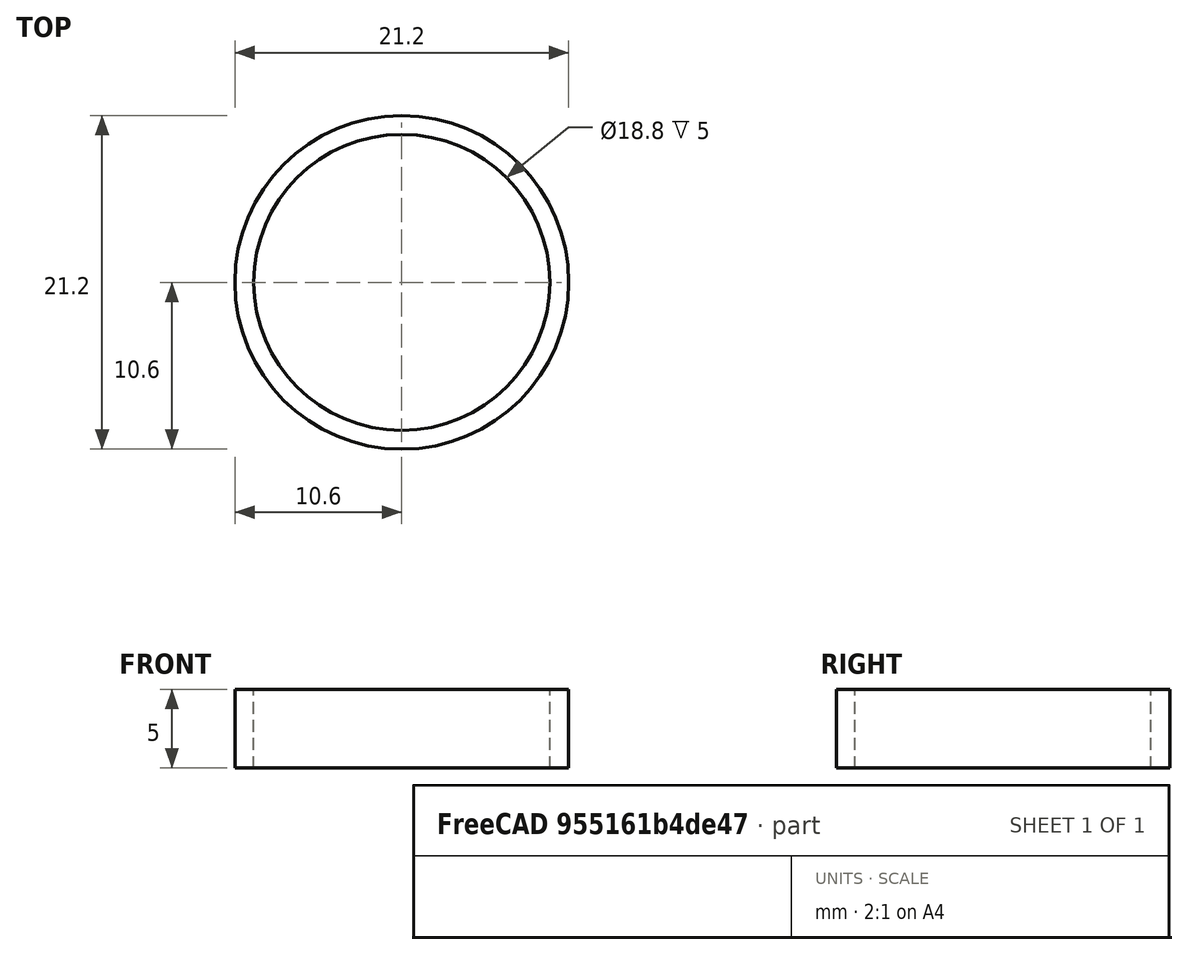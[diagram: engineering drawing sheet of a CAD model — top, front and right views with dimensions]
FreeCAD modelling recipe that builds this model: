
FCSTD DOCUMENT  (FreeCAD 0.20R29177 +426 (Git))
Label: Mag_AG_Outer
License: All rights reserved
LicenseURL: http://en.wikipedia.org/wiki/All_rights_reserved
objects: Sketcher::SketchObject×1, PartDesign::Revolution×1, PartDesign::Body×1
note: 4 computed .brp shape members not serialized (recipe doc carries the construction recipe); baked Part::Feature solids carry a one-line shape summary decoded from their .brp

FEATURE [Sketcher::SketchObject] Sketch
  FullyConstrained = true
  MapMode = 5
  Placement = pos=(0,0,0) rot=(1,0,0;1.5708rad)
  Support = -> [XZ_Plane]
  sketch-geometry (4):
    g0: LineSegment StartX=-9.4 StartY=0 StartZ=0 EndX=-9.4 EndY=5 EndZ=0
    g1: LineSegment StartX=-10.6 StartY=5 StartZ=0 EndX=-10.6 EndY=0 EndZ=0
    g2: LineSegment StartX=-9.4 StartY=0 StartZ=0 EndX=-10.6 EndY=0 EndZ=0
    g3: LineSegment StartX=-9.4 StartY=5 StartZ=0 EndX=-10.6 EndY=5 EndZ=0
  constraints (12):
    c: Vertical(g0)
    c: Vertical(g1)
    c: Coincident(g2,g0)
    c: Coincident(g2,g1)
    c: Coincident(g3,g0)
    c: Coincident(g3,g1)
    c: Horizontal(g3)
    c: Horizontal(g2)
    c: DistanceX(g2,g2) = 1.2
    c: DistanceY(g0,g0) = 5
    c: Horizontal(g-1,g0)
    c: DistanceX(g1,g-1) = 10.6
FEATURE [PartDesign::Revolution] Revolution
  Angle = 360
  Axis = (0,-2e-16,1)
  Base = (0,0,0)
  Placement = pos=(0,0,0) rot=(1,0,0;1.5708rad)
  Profile = -> Sketch
  ReferenceAxis = -> Sketch [V_Axis]
FEATURE [PartDesign::Body] Body
  Group = -> [Sketch,Revolution]
  Origin = -> Origin
  Tip = -> Revolution
